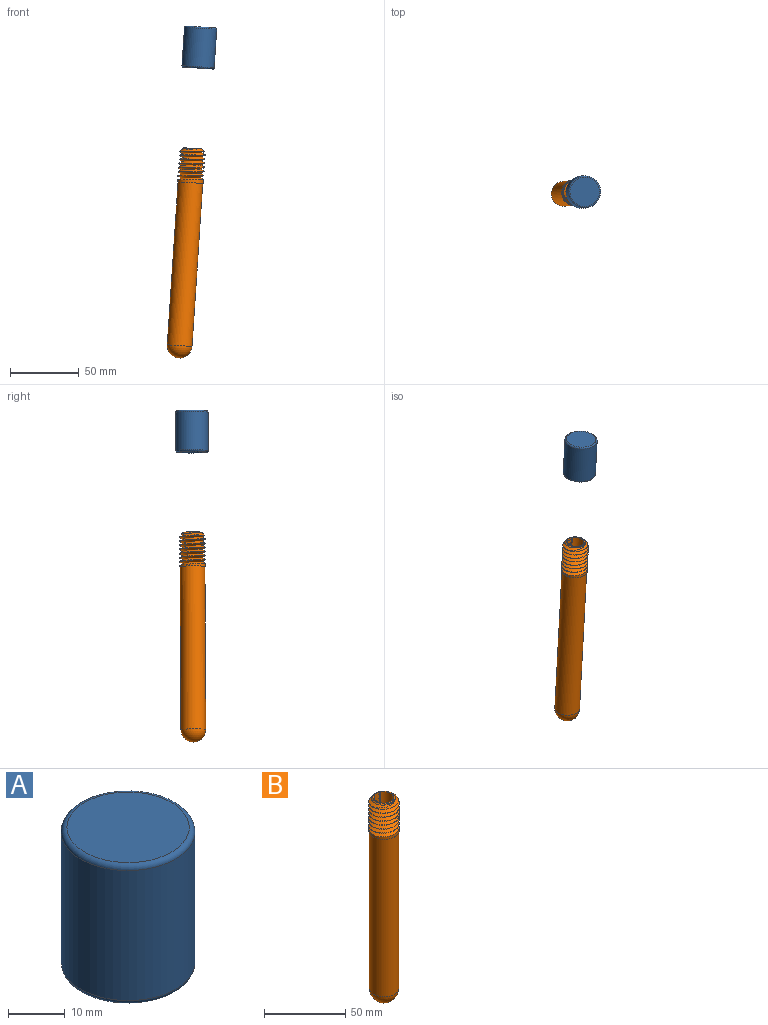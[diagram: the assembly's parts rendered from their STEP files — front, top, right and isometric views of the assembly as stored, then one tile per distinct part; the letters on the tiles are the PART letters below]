
ASSEMBLY  parts=2 mates=1
PART A: 12 faces, bbox 25.4x25.4x31.5 mm
  f0: cylinder r=11.75mm len=28mm, axis (0,0,1), area 2067.2mm2, adj f10,f11
  f1: plane 21.5x21.5mm, normal (0,0,-1), area 33mm2, adj f6,f11
  f2: plane 21.5x21.5mm, normal (0,0,1), area 363.1mm2, adj f10
  f3: cylinder r=7.25mm len=22mm, axis (0,0,-1), area 8.1mm2, adj f4,f5,f7,f8,f9
  f4: plane 14.5x14.5mm, normal (0,0,-1), area 165.1mm2, adj f3
  f5: cone r=7.25mm half-angle=45deg, axis (0,0,-1), area 0.1mm2, adj f3,f6,f8
  f6: cone r=7.25mm half-angle=45deg, axis (0,0,-1), area 142.8mm2, adj f1,f5,f8,f9
  f7: plane 2.95x2.55mm, normal (0,-1,0), area 3.8mm2, adj f3,f8,f9
  f8: bspline ~25.48x22.64mm, area 1188.2mm2, adj f3,f5,f6,f7,f9
  f9: bspline ~24.98x22.64mm, area 1113mm2, adj f3,f6,f7,f8
  f10: torus R=10.75mm, axis (0,0,1), area 112.4mm2, adj f0,f2
  f11: torus R=10.75mm, axis (0,0,1), area 112.4mm2, adj f0,f1
PART B: 18 faces, bbox 18.8x21.7x154.8 mm
  f0: plane 4.49x0.38mm, normal (0,0,1), area 1.1mm2, adj f14,f17
  f1: cylinder r=9.38mm len=22.5mm, axis (0,0,1), area 130.1mm2, adj f2,f4,f5,f6,f17
  f2: plane 18.75x18.75mm, normal (0,0,-1), area 21.7mm2, adj f1,f8
  f3: plane 13.75x13.28mm, normal (0,0,1), area 30.9mm2, adj f9,f11,f12,f17
  f4: plane 2.75x2.38mm, normal (0,1,0), area 3.3mm2, adj f1,f5,f6
  f5: bspline ~25.38x21.65mm, area 1009.1mm2, adj f1,f4,f6,f17
  f6: bspline ~25.88x21.65mm, area 1090.1mm2, adj f1,f4,f5,f17
  f7: sphere r=9mm, area 508.9mm2, adj f8
  f8: cylinder r=9mm len=119mm, axis (0,0,1), area 6729.3mm2, adj f2,f7
  f9: cylinder r=6mm len=128.75mm, axis (0,0,1), area 4559.8mm2, adj f3,f11,f12,f13,f15
  f10: cylinder r=2.75mm len=13mm, axis (0,0,1), area 224.6mm2, adj f15,f16
  f11: plane 57x1.05mm, normal (1,0,0), area 59.6mm2, adj f3,f9,f13,f14,f17
  f12: plane 57x1.05mm, normal (-1,0,0), area 59.6mm2, adj f3,f9,f13,f14,f17
  f13: plane 5x1.05mm, normal (0,0,1), area 3.4mm2, adj f9,f11,f12,f14
  f14: plane 57x5mm, normal (0,-1,0), area 285mm2, adj f0,f11,f12,f13,f17
  f15: cone r=2.75mm half-angle=45deg, axis (0,0,1), area 126.3mm2, adj f9,f10
  f16: plane 5.5x5.5mm, normal (0,0,1), area 23.8mm2, adj f10
  f17: cone r=6.88mm half-angle=45deg, axis (0,0,-1), area 97.2mm2, adj f0,f1,f3,f5,f6,f11,f12,f14
PLACE A rot(axis=(-0.04,0.1,-0.99),34.3deg) t=(212.48,-28.33,-233)mm
PLACE B rot(axis=(-0.02,0.63,0.77),6deg) t=(206.64,-28.72,-321.48)mm
MATE cylindrical A.f0 <-> B.f1  axis (-0.07,0,-1) through (212.15,-28.35,-237.99)mm
